# Revit family: TV302-C-1.5
name_source: partatom
category: Aparatos sanitarios
units: mm (PartAtom-declared; Revit-internal decimal feet)

## family parameters
Compartido = Sí
Corte con vacíos al cargar = No
Cota de conector redondo = Diámetro de uso
Número OmniClass = 23.45.00.00
Punto de cálculo de habitación = Sí
Se basa en plano de trabajo = Sí
Siempre vertical = Sí
Tipo de pieza = Normal
Título OmniClass = Sanitary, Laundry, and Cleaning Equipment

## types (1)
- TV-302-C
    Chrome = Brass Chromed
    Comentarios de tipo = Línea Electronica
    Conexión AF = Sí
    Connection = ½" - 14 NPSM
    Descripción = Llave de Lavabo Electrónica de Sensor de Corriente
    Detection Range = 9.8 (25 cm)
    Elevación por Defecto = 1"
    Elevación por defecto = 48"
    Fabricante = Helvex
    Features = Sensor infrarrojo, Distancia de detección 25cm (ajuste de fábrica), Fuente de alimentación regulada clase 2, Entrada: 115 - 230 Vca, 50/60 Hz, Salida: 6V cc/200mA
    Feeding Voltage = 6 V
    Imagen de tipo = <Ninguno>
    Max. Working Pressure = 85.3 psi
    Min. Working Pressure = 11.3 psi
    Modelo = TV-302-C
    Operación = Active la salida colocando su mano dentro de la zona de detección.
    Total Height = 11"
    Total Lenght = 0"
    Total Width = 9"

## geometry (parser evidence)
native form markers: Sweep x3
no freeform markers — native parametric forms only
